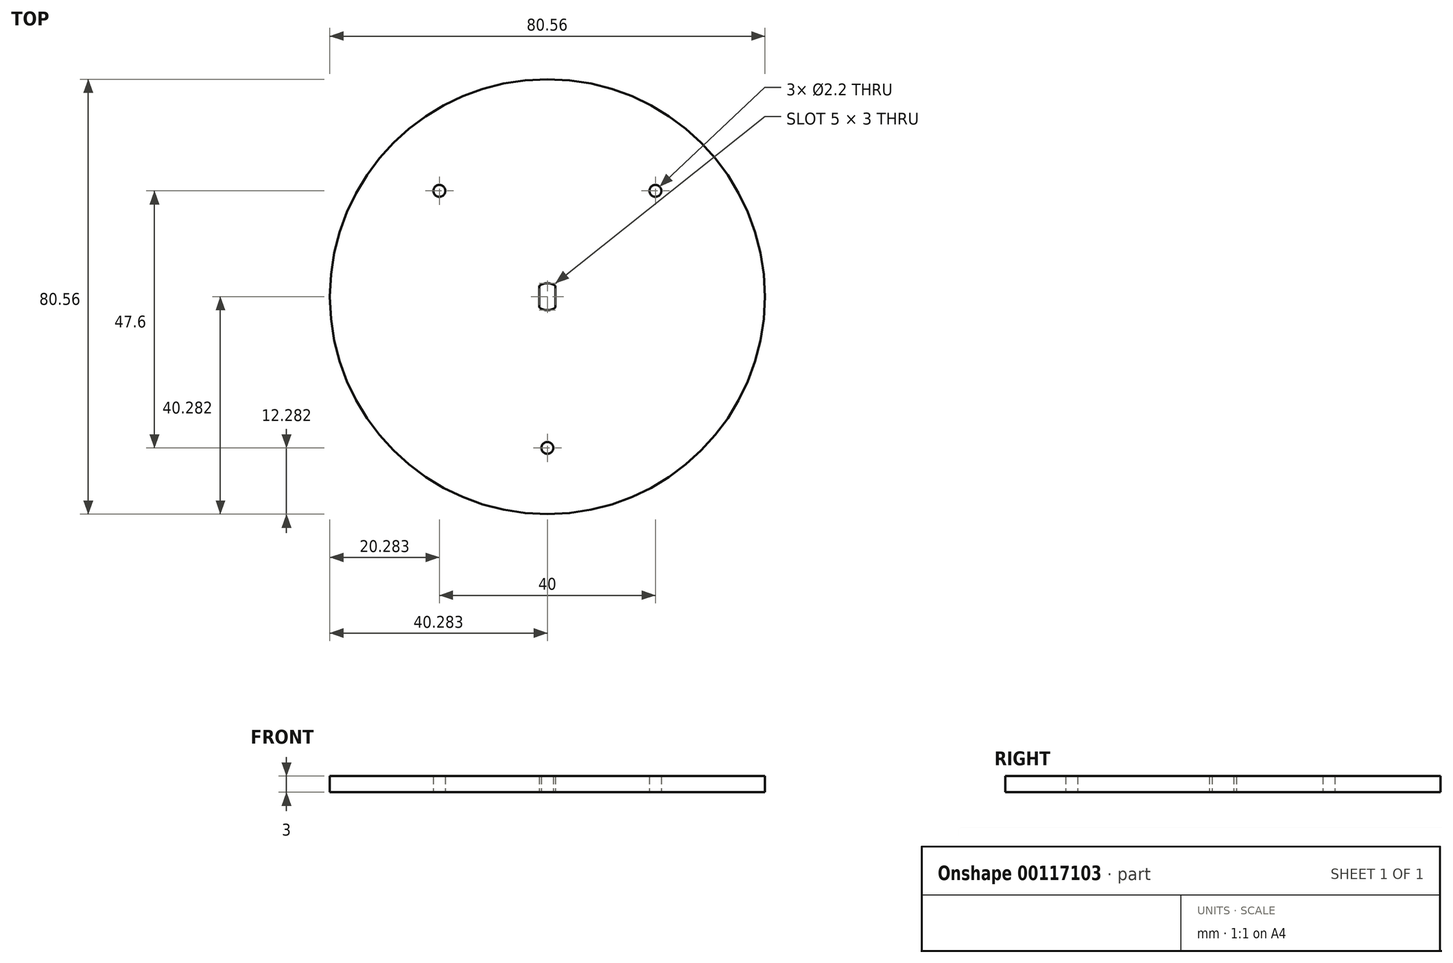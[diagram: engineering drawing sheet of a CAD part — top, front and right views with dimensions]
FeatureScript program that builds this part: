
annotation { "Feature Type Name" : "Feature", "Feature Type Description" : "" }
export const myFeature = defineFeature(function(context is Context, id is Id, definition is map)
    precondition{}
    {
        {
            var Q0;
            Q0=qCreatedBy(makeId("Top.planeOp"),FACE);
            var sketch = newSketch(context, id + "F0", { "sketchPlane" : qUnion([Q0])});
            skCircle(sketch, "E0", {"center": v(4.35, 38.44) * mm, "radius": 1.1 * mm});
            skCircle(sketch, "E1", {"center": v(-35.65, 38.44) * mm, "radius": 1.1 * mm});
            skCircle(sketch, "E2", {"center": v(-15.65, -9.16) * mm, "radius": 1.1 * mm});
            skCircle(sketch, "E3", {"center": v(-15.65, 18.84) * mm, "radius": 40.28 * mm});
            skLineSegment(sketch, "E4.left", {"start": v(-14.15, 16.84) * mm, "end": v(-14.15, 20.84) * mm});
            skLineSegment(sketch, "E4.right", {"start": v(-17.15, 16.84) * mm, "end": v(-17.15, 20.84) * mm});
            skArc(sketch, "E5", {"start": v(-14.15, 20.84) * mm, "mid": v(-15.65, 21.34) * mm, "end": v(-17.15, 20.84) * mm});
            skPoint(sketch, "E4.top.end.orphan", {"position": v(-17.15, 22.84) * mm});
            skPoint(sketch, "E6.orphan", {"position": v(-14.15, 22.84) * mm});
            skPoint(sketch, "E4.bottom.start.orphan", {"position": v(-14.15, 14.84) * mm});
            skPoint(sketch, "E7.orphan", {"position": v(-17.15, 14.84) * mm});
            skArc(sketch, "E8.trimOffspring", {"start": v(-17.15, 16.84) * mm, "mid": v(-15.65, 16.34) * mm, "end": v(-14.15, 16.84) * mm});
            skSolve(sketch);
        }
        {
            var Q0;
            Q0=makeQuery(id+"F0.imprint","IMPRINT",FACE,{"disambiguationData":[TD([[makeQuery(id+"F0.imprint","IMPRINT",EDGE,{"derivedFrom":sQuery(id+"F0.wireOp",EDGE,"E0")}),-1.0]])]});
            extrude(context, id + "F1", {"entities" : qUnion([Q0]), "depth" : 3 * mm});
        }
    });
